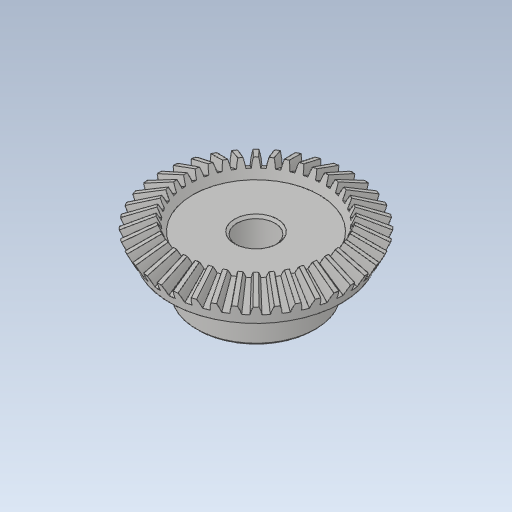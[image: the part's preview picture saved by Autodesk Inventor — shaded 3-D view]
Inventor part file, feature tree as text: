
AUTODESK INVENTOR PART (.ipt)
format: ipt  version: 2024 (Build 280153000, 153)  size: 1,019,904 bytes
history: native  units: mm
features: other x21, sketch x4, revolve x2, loft x1
ambient origin geometry x8: Origin, YZ Plane, XZ Plane, XY Plane, X Axis, Y Axis, Z Axis, Center Point
bodies: Solid1 (feature_tree)
feature tree (28):
  loft  "Loft1"
  revolve  "Revolution1"  Angle=360.0deg
  revolve  "Revolution2"  [1 undecoded]
  other  "IP2_XY"
  other  "IP2_YZ"
  other  "IP2_ZX"
  other  "IP2_X"
  other  "IP2_Y"
  other  "IP2_Z"
  other  "IP2_Center"
  other  "dummy_XY"
  other  "dummy_YZ"
  other  "dummy_ZX"
  other  "dummy_X"
  other  "dummy_Y"
  other  "dummy_Z"
  other  "dummy_Center"
  other  "r_XY"
  other  "r_YZ"
  other  "r_ZX"
  other  "r_X"
  other  "r_Y"
  other  "r_Z"
  other  "r_Center"
  sketch  "Sketch_5"  dims[d0=0.0mm d1=90.0deg d2=0.0mm d3=90.0deg]
  sketch  "Sketch_6"  dims[d4=360.0deg d5=360.0deg]
  sketch  "Sketch_7"
  sketch  "Sketch_8"
note: 1 required parameter value undecoded (feature->parameter linkage not recoverable at this tier; creation-order binding heuristic only, values carry confidence <= 0.55)
